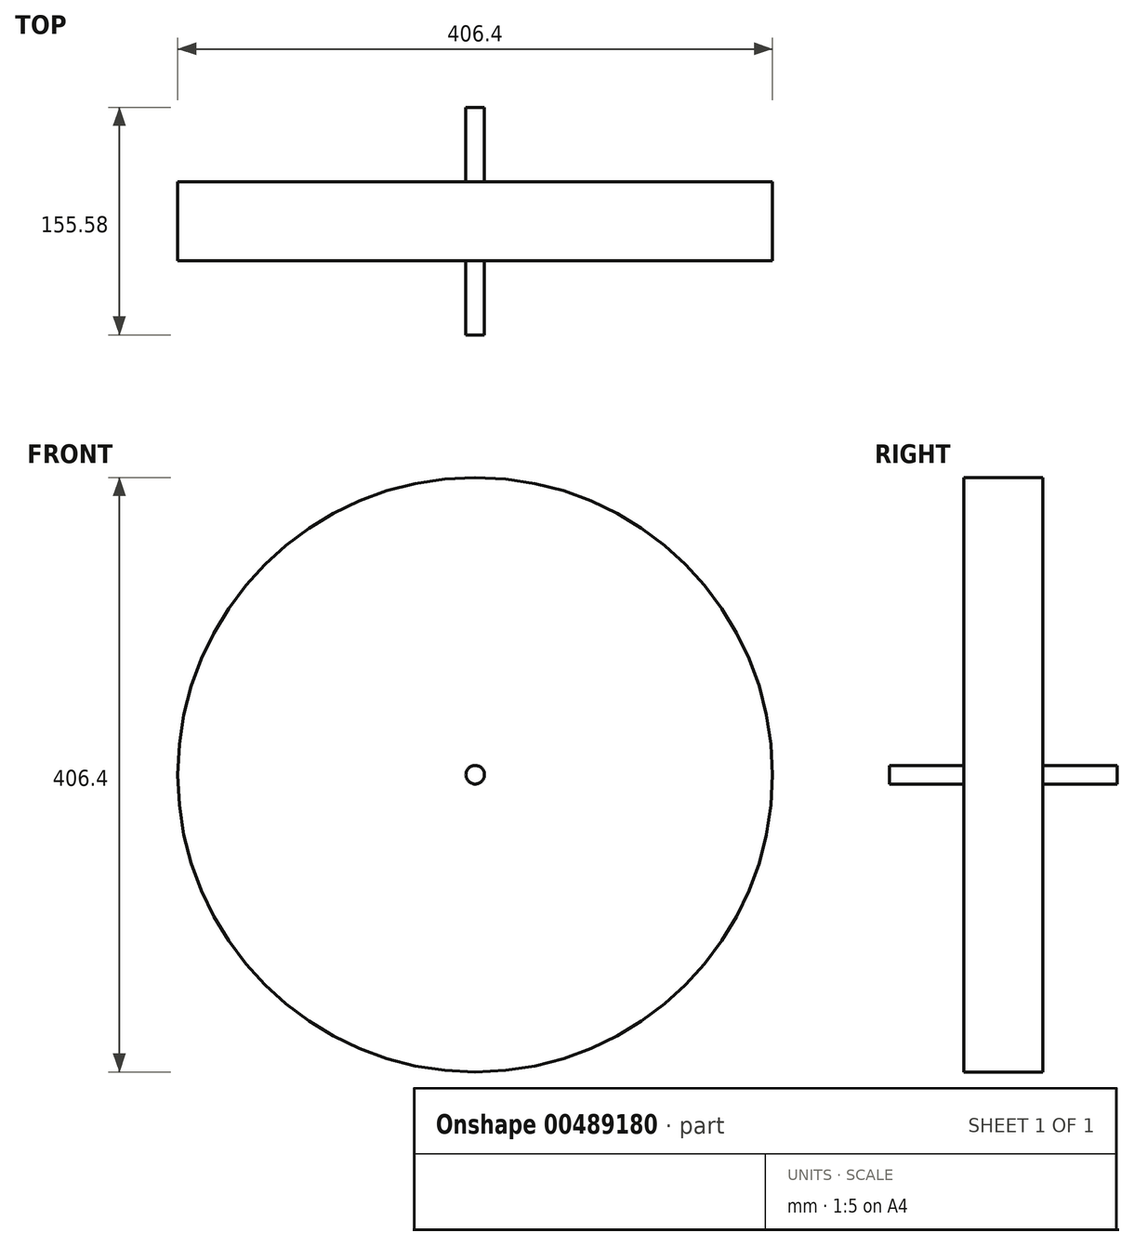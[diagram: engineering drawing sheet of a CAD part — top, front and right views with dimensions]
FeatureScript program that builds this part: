
annotation { "Feature Type Name" : "Feature", "Feature Type Description" : "" }
export const myFeature = defineFeature(function(context is Context, id is Id, definition is map)
    precondition{}
    {
        {
            var Q0;
            Q0=qCreatedBy(makeId("Front.planeOp"),FACE);
            var sketch = newSketch(context, id + "F0", { "sketchPlane" : qUnion([Q0])});
            skCircle(sketch, "E0", {"center": v(0, 0) * mm, "radius": 203.2 * mm});
            skCircle(sketch, "E1", {"center": v(0, 0) * mm, "radius": 6.35 * mm});
            skSolve(sketch);
        }
        {
            var Q0;
            Q0=makeQuery(id+"F0.imprint","IMPRINT",FACE,{"disambiguationData":[TD([[makeQuery(id+"F0.imprint","IMPRINT",EDGE,{"derivedFrom":sQuery(id+"F0.wireOp",EDGE,"E1")}),1.0]])]});
            var Q1;
            Q1=makeQuery(id+"F0.imprint","IMPRINT",FACE,{"disambiguationData":[TD([[makeQuery(id+"F0.imprint","IMPRINT",EDGE,{"derivedFrom":sQuery(id+"F0.wireOp",EDGE,"E0")}),1.0]])]});
            extrude(context, id + "F1", {"entities" : qUnion([Q0, Q1]), "depth" : 53.97 * mm, "offsetDistance" : 25.4 * mm});
        }
        {
            var Q0;
            Q0=makeQuery(id+"F0.imprint","IMPRINT",FACE,{"disambiguationData":[TD([[makeQuery(id+"F0.imprint","IMPRINT",EDGE,{"derivedFrom":sQuery(id+"F0.wireOp",EDGE,"E1")}),1.0]])]});
            extrude(context, id + "F2", {"entities" : qUnion([Q0]), "operationType" : NewBodyOperationType.ADD, "depth" : 104.77 * mm, "offsetDistance" : 25.4 * mm, "hasSecondDirection" : true, "secondDirectionOppositeDirection" : true, "secondDirectionDepth" : 50.8 * mm});
        }
    });
